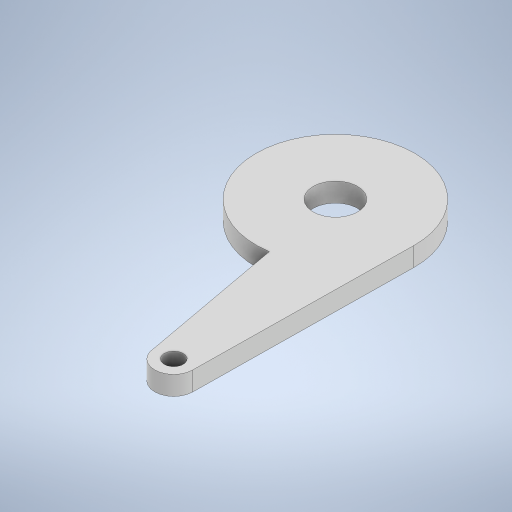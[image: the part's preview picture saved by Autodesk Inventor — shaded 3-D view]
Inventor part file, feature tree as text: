
AUTODESK INVENTOR PART (.ipt)
format: ipt  version: 2023 (Build 270158000, 158)  size: 246,784 bytes
history: native  units: mm
features: other x1, extrude x1, sketch x1
ambient origin geometry x8: Origin, YZ Plane, XZ Plane, XY Plane, X Axis, Y Axis, Z Axis, Center Point
bodies: Body1 (feature_tree)
feature tree (3):
  other  "Sólido1"
  extrude  "Extrusión1"  Depth=3.0mm
  sketch  "Boceto1"  dims[d0=6.0mm d1=3.0mm d3=12.5mm d4=50.0mm d5=7.0mm d6=3.0mm d7=0.0mm]
